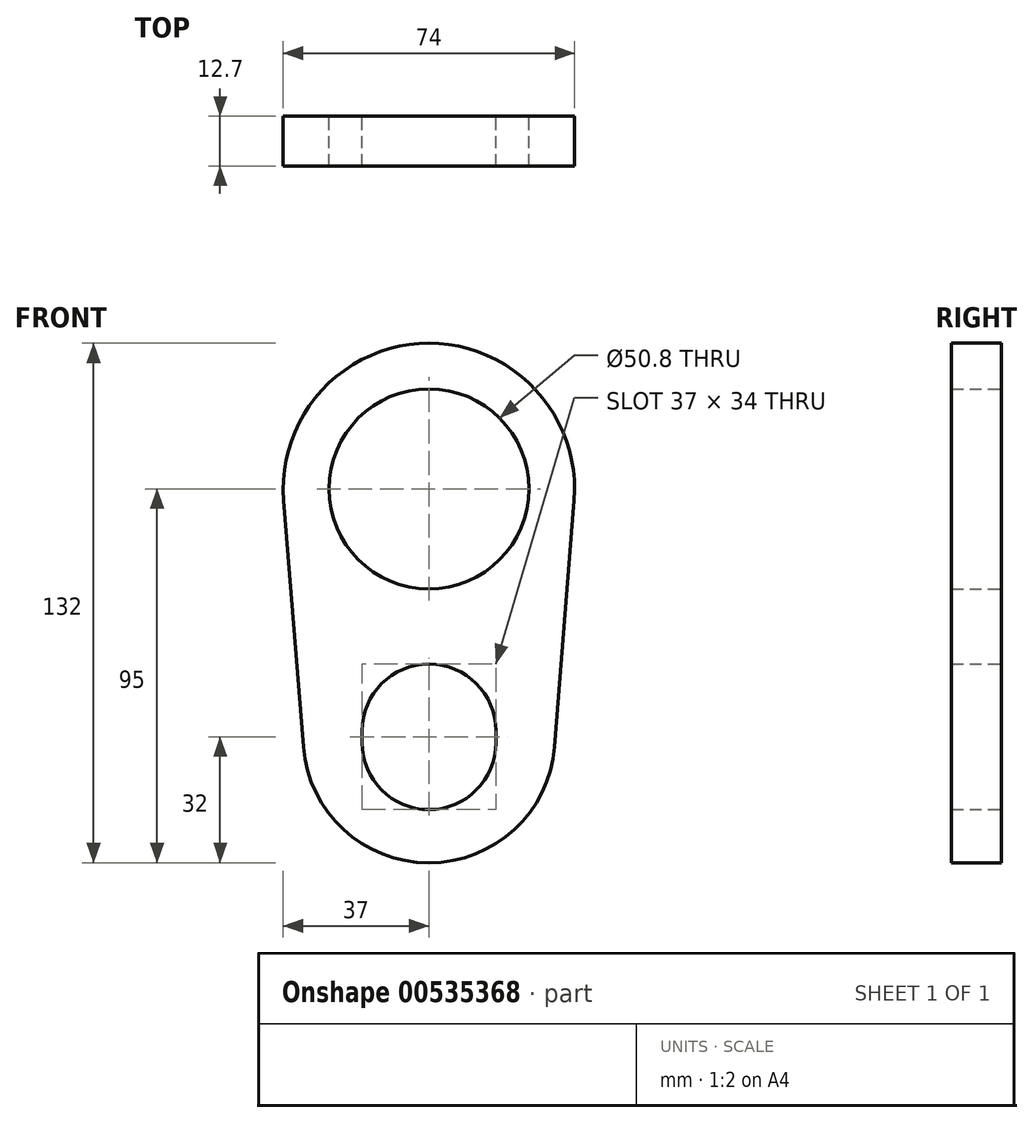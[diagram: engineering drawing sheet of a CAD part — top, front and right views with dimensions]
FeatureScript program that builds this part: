
annotation { "Feature Type Name" : "Feature", "Feature Type Description" : "" }
export const myFeature = defineFeature(function(context is Context, id is Id, definition is map)
    precondition{}
    {
        {
            var Q0;
            Q0=qCreatedBy(makeId("Front.planeOp"),FACE);
            var sketch = newSketch(context, id + "F0", { "sketchPlane" : qUnion([Q0])});
            skArc(sketch, "E0", {"start": v(36.88, -2.94) * mm, "mid": v(0, 37) * mm, "end": v(-36.88, -2.94) * mm});
            skLineSegment(sketch, "E1", {"start": v(-36.88, -2.94) * mm, "end": v(-31.9, -65.54) * mm});
            skLineSegment(sketch, "E2", {"start": v(0, 0) * mm, "end": v(0, -63) * mm, "construction": true});
            skLineSegment(sketch, "E3.MirrorCS", {"start": v(36.88, -2.94) * mm, "end": v(31.9, -65.54) * mm});
            skArc(sketch, "E4.trimOffspring", {"start": v(-31.9, -65.54) * mm, "mid": v(0, -95) * mm, "end": v(31.9, -65.54) * mm});
            skCircle(sketch, "E5", {"center": v(0, 0) * mm, "radius": 25.4 * mm});
            skLineSegment(sketch, "E6", {"start": v(0, -61.5) * mm, "end": v(0, -64.5) * mm});
            skArc(sketch, "E7.0.startCap", {"start": v(-17, -61.5) * mm, "mid": v(0, -44.5) * mm, "end": v(17, -61.5) * mm});
            skArc(sketch, "E7.0.endCap", {"start": v(17, -64.5) * mm, "mid": v(0, -81.5) * mm, "end": v(-17, -64.5) * mm});
            skLineSegment(sketch, "E7.0.left", {"start": v(17, -61.5) * mm, "end": v(17, -64.5) * mm});
            skLineSegment(sketch, "E7.0.right", {"start": v(-17, -61.5) * mm, "end": v(-17, -64.5) * mm});
            skSolve(sketch);
        }
        {
            var Q0;
            Q0=qSketchRegion(id+"F0",true);
            extrude(context, id + "F1", {"entities" : qUnion([Q0]), "depth" : 12.7 * mm, "offsetDistance" : 25.4 * mm});
        }
    });
